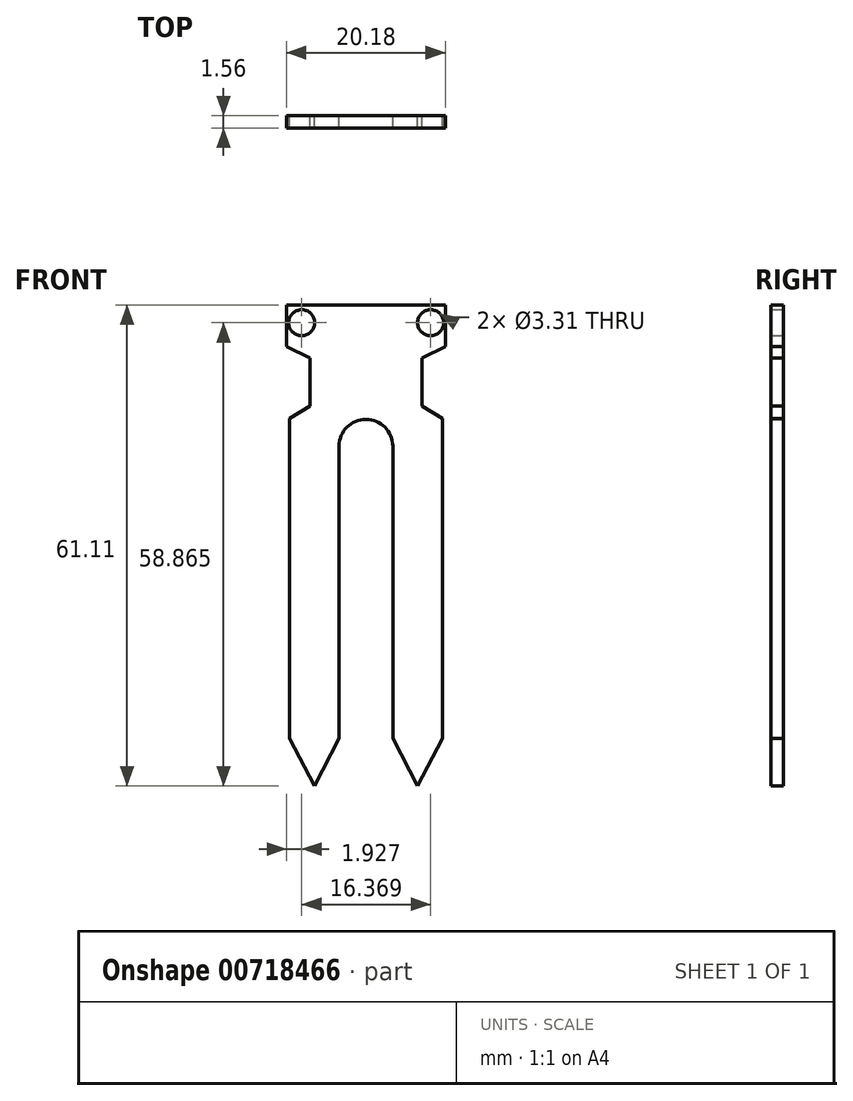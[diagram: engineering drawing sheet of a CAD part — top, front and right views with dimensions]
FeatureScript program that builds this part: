
annotation { "Feature Type Name" : "Feature", "Feature Type Description" : "" }
export const myFeature = defineFeature(function(context is Context, id is Id, definition is map)
    precondition{}
    {
        {
            var Q0;
            Q0=qCreatedBy(makeId("Front.planeOp"),FACE);
            var sketch = newSketch(context, id + "F0", { "sketchPlane" : qUnion([Q0])});
            skLineSegment(sketch, "E0", {"start": v(0, 0) * mm, "end": v(10.09, 0) * mm});
            skLineSegment(sketch, "E1.MirrorCS", {"start": v(0, 0) * mm, "end": v(-10.09, 0) * mm});
            skLineSegment(sketch, "E2", {"start": v(-9.72, -17.92) * mm, "end": v(-9.72, -55.05) * mm});
            skLineSegment(sketch, "E3", {"start": v(9.72, -17.92) * mm, "end": v(9.72, -55.05) * mm});
            skLineSegment(sketch, "E4", {"start": v(-9.72, -55.05) * mm, "end": v(-6.56, -61.11) * mm});
            skLineSegment(sketch, "E5", {"start": v(-6.56, -61.11) * mm, "end": v(-3.4, -55.05) * mm});
            skLineSegment(sketch, "E6", {"start": v(9.72, -55.05) * mm, "end": v(6.56, -61.11) * mm});
            skLineSegment(sketch, "E7", {"start": v(6.57, -61.11) * mm, "end": v(3.41, -55.05) * mm});
            skLineSegment(sketch, "E8", {"start": v(-3.4, -55.05) * mm, "end": v(-3.41, -17.92) * mm});
            skLineSegment(sketch, "E9", {"start": v(3.41, -55.05) * mm, "end": v(3.4, -17.92) * mm});
            skArc(sketch, "E10", {"start": v(3.4, -17.92) * mm, "mid": v(0, -14.51) * mm, "end": v(-3.4, -17.92) * mm});
            skLineSegment(sketch, "E11", {"start": v(-7.1, -6.73) * mm, "end": v(-7.1, -12.8) * mm});
            skLineSegment(sketch, "E12", {"start": v(7.1, -6.73) * mm, "end": v(7.1, -12.8) * mm});
            skLineSegment(sketch, "E13", {"start": v(-10.09, 0) * mm, "end": v(-10.09, -5.26) * mm});
            skLineSegment(sketch, "E14", {"start": v(10.09, 0) * mm, "end": v(10.09, -5.26) * mm});
            skLineSegment(sketch, "E15", {"start": v(-10.09, -5.26) * mm, "end": v(-7.1, -6.73) * mm});
            skLineSegment(sketch, "E16", {"start": v(10.09, -5.26) * mm, "end": v(7.1, -6.73) * mm});
            skLineSegment(sketch, "E17", {"start": v(-9.72, -17.92) * mm, "end": v(-9.72, -14.43) * mm});
            skLineSegment(sketch, "E18", {"start": v(9.72, -17.92) * mm, "end": v(9.72, -14.43) * mm});
            skLineSegment(sketch, "E19", {"start": v(-7.1, -12.8) * mm, "end": v(-9.72, -14.43) * mm});
            skLineSegment(sketch, "E20", {"start": v(7.1, -12.8) * mm, "end": v(9.72, -14.43) * mm});
            skCircle(sketch, "E21", {"center": v(-8.16, -2.24) * mm, "radius": 1.66 * mm});
            skCircle(sketch, "E22", {"center": v(8.2, -2.24) * mm, "radius": 1.66 * mm});
            skSolve(sketch);
        }
        {
            var Q0;
            Q0 = qSketchRegion(id + "F0", true);
            extrude(context, id + "F1", {"entities" : qUnion([Q0]), "depth" : 1.56 * mm, "offsetDistance" : 25 * mm});
        }
    });
